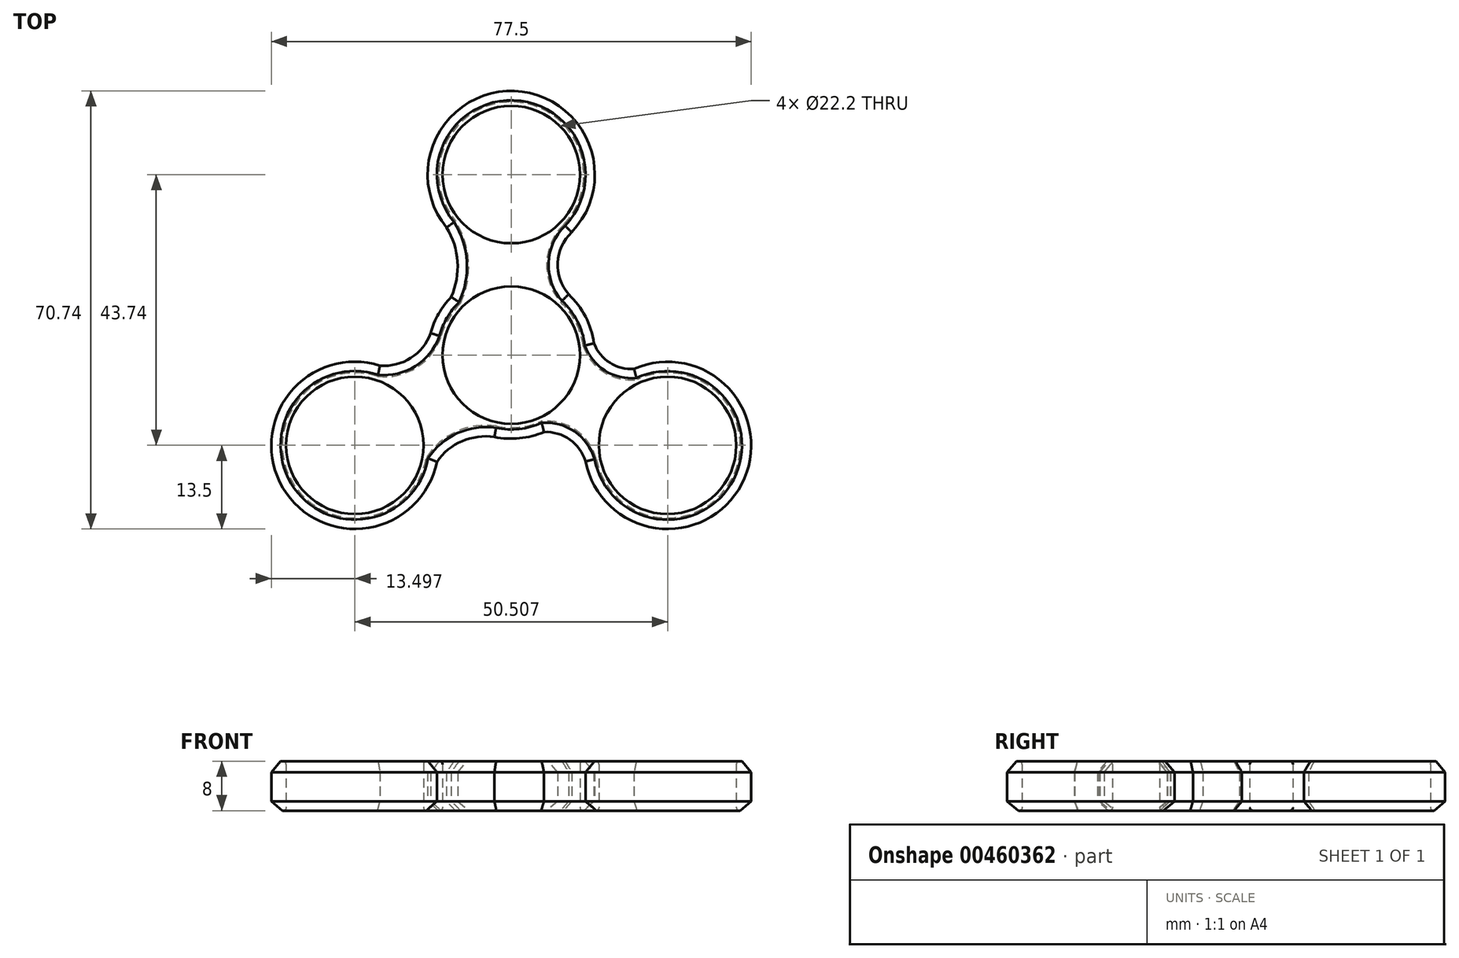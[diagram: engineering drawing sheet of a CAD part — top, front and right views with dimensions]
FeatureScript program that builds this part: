
annotation { "Feature Type Name" : "Feature", "Feature Type Description" : "" }
export const myFeature = defineFeature(function(context is Context, id is Id, definition is map)
    precondition{}
    {
        {
            var Q0;
            Q0=qCreatedBy(makeId("Top.planeOp"),FACE);
            var sketch = newSketch(context, id + "F0", { "sketchPlane" : qUnion([Q0])});
            skCircle(sketch, "E0", {"center": v(0, 0) * mm, "radius": 11.1 * mm});
            skCircle(sketch, "E1", {"center": v(0, 0) * mm, "radius": 13.5 * mm});
            skCircle(sketch, "E2", {"center": v(0, 29.16) * mm, "radius": 11.1 * mm});
            skCircle(sketch, "E3", {"center": v(0, 29.16) * mm, "radius": 13.5 * mm});
            skCircle(sketch, "E4.1.0", {"center": v(-25.25, -14.58) * mm, "radius": 11.1 * mm});
            skCircle(sketch, "E4.2.0", {"center": v(25.25, -14.58) * mm, "radius": 11.1 * mm});
            skCircle(sketch, "E5.1.0", {"center": v(-25.25, -14.58) * mm, "radius": 13.5 * mm});
            skCircle(sketch, "E5.2.0", {"center": v(25.25, -14.58) * mm, "radius": 13.5 * mm});
            skArc(sketch, "E6", {"start": v(-9.69, 9.4) * mm, "mid": v(-8.68, 15.1) * mm, "end": v(-10.44, 20.6) * mm});
            skArc(sketch, "E7", {"start": v(9.76, 19.84) * mm, "mid": v(7.53, 14.92) * mm, "end": v(9.27, 9.81) * mm});
            skArc(sketch, "E8", {"start": v(-21.2, -1.7) * mm, "mid": v(-16.22, -0.47) * mm, "end": v(-13.03, 3.55) * mm});
            skArc(sketch, "E9", {"start": v(-2.71, -13.22) * mm, "mid": v(-7.94, -13.91) * mm, "end": v(-12.02, -17.25) * mm});
            skArc(sketch, "E10", {"start": v(12, -17.17) * mm, "mid": v(9.46, -13.64) * mm, "end": v(5.28, -12.43) * mm});
            skArc(sketch, "E11", {"start": v(13.36, 1.91) * mm, "mid": v(15.92, -1.22) * mm, "end": v(19.84, -2.21) * mm});
            skSolve(sketch);
        }
        {
            var Q0;
            Q0=makeQuery(id+"F0.imprint","IMPRINT",FACE,{"disambiguationData":[TD([[makeQuery(id+"F0.imprint","IMPRINT",EDGE,{"derivedFrom":sQuery(id+"F0.wireOp",EDGE,"E2")}),-1.0]])]});
            var Q1;
            Q1=makeQuery(id+"F0.imprint","IMPRINT",FACE,{"disambiguationData":[TD([[makeQuery(id+"F0.imprint","IMPRINT",EDGE,{"derivedFrom":sQuery(id+"F0.wireOp",EDGE,"E0")}),-1.0]])]});
            var Q2;
            Q2=makeQuery(id+"F0.imprint","IMPRINT",FACE,{"disambiguationData":[TD([[makeQuery(id+"F0.imprint","IMPRINT",EDGE,{"derivedFrom":sQuery(id+"F0.wireOp",EDGE,"E4.1.0")}),-1.0]])]});
            var Q3;
            Q3=makeQuery(id+"F0.imprint","IMPRINT",FACE,{"disambiguationData":[TD([[makeQuery(id+"F0.imprint","IMPRINT",EDGE,{"derivedFrom":sQuery(id+"F0.wireOp",EDGE,"E4.2.0")}),-1.0]])]});
            var Q4;
            {var subQ0=sQuery(id+"F0.wireOp",EDGE,"E10");Q4=makeQuery(id+"F0.imprint","IMPRINT",FACE,{"disambiguationData":[TD([[makeQuery(id+"F0.imprint","IMPRINT",EDGE,{"derivedFrom":subQ0}),-1.0]])]});}
            var Q5;
            {var subQ0=sQuery(id+"F0.wireOp",EDGE,"E8");Q5=makeQuery(id+"F0.imprint","IMPRINT",FACE,{"disambiguationData":[TD([[makeQuery(id+"F0.imprint","IMPRINT",EDGE,{"derivedFrom":subQ0}),-1.0]])]});}
            var Q6;
            {var subQ0=sQuery(id+"F0.wireOp",EDGE,"E6");Q6=makeQuery(id+"F0.imprint","IMPRINT",FACE,{"disambiguationData":[TD([[makeQuery(id+"F0.imprint","IMPRINT",EDGE,{"derivedFrom":subQ0}),-1.0]])]});}
            extrude(context, id + "F1", {"entities" : qUnion([Q0, Q1, Q2, Q3, Q4, Q5, Q6]), "depth" : 8 * mm});
        }
        {
            var Q0;
            Q0=makeQuery(id+"F1.opExtrude","CAP_EDGE",EDGE,{"disambiguationData":[OSD([sQuery(id+"F0.wireOp",EDGE,"E5.1.0")])],"isStart":false});
            var Q1;
            Q1=makeQuery(id+"F1.opExtrude","CAP_EDGE",EDGE,{"disambiguationData":[OSD([sQuery(id+"F0.wireOp",EDGE,"E9")])],"isStart":false});
            var Q2;
            Q2=makeQuery(id+"F1.opExtrude","CAP_EDGE",EDGE,{"disambiguationData":[OSD([sQuery(id+"F0.wireOp",EDGE,"E8")])],"isStart":false});
            var Q3;
            {var subQ0=sQuery(id+"F0.wireOp",EDGE,"E1");Q3=makeQuery(id+"F1.opExtrude","CAP_EDGE",EDGE,{"disambiguationData":[OSD([subQ0]),TDD([makeQuery(id+"F0.imprint","IMPRINT",EDGE,{"disambiguationData":[TD([[makeQuery(id+"F0.imprint","INTERSECT",VERTEX,{"derivedFrom":[subQ0,sQuery(id+"F0.wireOp",EDGE,"E6")]}),-1.0]])],"derivedFrom":subQ0})])],"isStart":false});}
            var Q4;
            Q4=makeQuery(id+"F1.opExtrude","CAP_EDGE",EDGE,{"disambiguationData":[OSD([sQuery(id+"F0.wireOp",EDGE,"E6")])],"isStart":false});
            var Q5;
            Q5=makeQuery(id+"F1.opExtrude","CAP_EDGE",EDGE,{"disambiguationData":[OSD([sQuery(id+"F0.wireOp",EDGE,"E3")])],"isStart":false});
            var Q6;
            Q6=makeQuery(id+"F1.opExtrude","CAP_EDGE",EDGE,{"disambiguationData":[OSD([sQuery(id+"F0.wireOp",EDGE,"E7")])],"isStart":false});
            var Q7;
            {var subQ0=sQuery(id+"F0.wireOp",EDGE,"E1");Q7=makeQuery(id+"F1.opExtrude","CAP_EDGE",EDGE,{"disambiguationData":[OSD([subQ0]),TDD([makeQuery(id+"F0.imprint","IMPRINT",EDGE,{"disambiguationData":[TD([[makeQuery(id+"F0.imprint","INTERSECT",VERTEX,{"derivedFrom":[subQ0,sQuery(id+"F0.wireOp",EDGE,"E7")]}),1.0]])],"derivedFrom":subQ0})])],"isStart":false});}
            var Q8;
            Q8=makeQuery(id+"F1.opExtrude","CAP_EDGE",EDGE,{"disambiguationData":[OSD([sQuery(id+"F0.wireOp",EDGE,"E11")])],"isStart":false});
            var Q9;
            Q9=makeQuery(id+"F1.opExtrude","CAP_EDGE",EDGE,{"disambiguationData":[OSD([sQuery(id+"F0.wireOp",EDGE,"E5.2.0")])],"isStart":false});
            var Q10;
            Q10=makeQuery(id+"F1.opExtrude","CAP_EDGE",EDGE,{"disambiguationData":[OSD([sQuery(id+"F0.wireOp",EDGE,"E10")])],"isStart":false});
            var Q11;
            {var subQ0=sQuery(id+"F0.wireOp",EDGE,"E1");Q11=makeQuery(id+"F1.opExtrude","CAP_EDGE",EDGE,{"disambiguationData":[OSD([subQ0]),TDD([makeQuery(id+"F0.imprint","IMPRINT",EDGE,{"disambiguationData":[TD([[makeQuery(id+"F0.imprint","INTERSECT",VERTEX,{"derivedFrom":[subQ0,sQuery(id+"F0.wireOp",EDGE,"E9")]}),-1.0]])],"derivedFrom":subQ0})])],"isStart":false});}
            chamfer(context, id + "F2", {"entities" : qUnion([Q0, Q1, Q2, Q3, Q4, Q5, Q6, Q7, Q8, Q9, Q10, Q11]), "chamferType" : ChamferType.OFFSET_ANGLE, "width" : 1.5 * mm, "oppositeDirection" : false, "angle" : 50 * degree, "tangentPropagation" : true});
        }
        {
            var Q0;
            Q0=makeQuery(id+"F1.opExtrude","CAP_EDGE",EDGE,{"disambiguationData":[OSD([sQuery(id+"F0.wireOp",EDGE,"E3")])],"isStart":true});
            var Q1;
            Q1=makeQuery(id+"F1.opExtrude","CAP_EDGE",EDGE,{"disambiguationData":[OSD([sQuery(id+"F0.wireOp",EDGE,"E6")])],"isStart":true});
            var Q2;
            Q2=makeQuery(id+"F1.opExtrude","CAP_EDGE",EDGE,{"disambiguationData":[OSD([sQuery(id+"F0.wireOp",EDGE,"E7")])],"isStart":true});
            var Q3;
            {var subQ0=sQuery(id+"F0.wireOp",EDGE,"E1");Q3=makeQuery(id+"F1.opExtrude","CAP_EDGE",EDGE,{"disambiguationData":[OSD([subQ0]),TDD([makeQuery(id+"F0.imprint","IMPRINT",EDGE,{"disambiguationData":[TD([[makeQuery(id+"F0.imprint","INTERSECT",VERTEX,{"derivedFrom":[subQ0,sQuery(id+"F0.wireOp",EDGE,"E7")]}),1.0]])],"derivedFrom":subQ0})])],"isStart":true});}
            var Q4;
            Q4=makeQuery(id+"F1.opExtrude","CAP_EDGE",EDGE,{"disambiguationData":[OSD([sQuery(id+"F0.wireOp",EDGE,"E11")])],"isStart":true});
            var Q5;
            Q5=makeQuery(id+"F1.opExtrude","CAP_EDGE",EDGE,{"disambiguationData":[OSD([sQuery(id+"F0.wireOp",EDGE,"E5.2.0")])],"isStart":true});
            var Q6;
            Q6=makeQuery(id+"F1.opExtrude","CAP_EDGE",EDGE,{"disambiguationData":[OSD([sQuery(id+"F0.wireOp",EDGE,"E10")])],"isStart":true});
            var Q7;
            {var subQ0=sQuery(id+"F0.wireOp",EDGE,"E1");Q7=makeQuery(id+"F1.opExtrude","CAP_EDGE",EDGE,{"disambiguationData":[OSD([subQ0]),TDD([makeQuery(id+"F0.imprint","IMPRINT",EDGE,{"disambiguationData":[TD([[makeQuery(id+"F0.imprint","INTERSECT",VERTEX,{"derivedFrom":[subQ0,sQuery(id+"F0.wireOp",EDGE,"E9")]}),-1.0]])],"derivedFrom":subQ0})])],"isStart":true});}
            var Q8;
            {var subQ0=sQuery(id+"F0.wireOp",EDGE,"E1");Q8=makeQuery(id+"F1.opExtrude","CAP_EDGE",EDGE,{"disambiguationData":[OSD([subQ0]),TDD([makeQuery(id+"F0.imprint","IMPRINT",EDGE,{"disambiguationData":[TD([[makeQuery(id+"F0.imprint","INTERSECT",VERTEX,{"derivedFrom":[subQ0,sQuery(id+"F0.wireOp",EDGE,"E6")]}),-1.0]])],"derivedFrom":subQ0})])],"isStart":true});}
            var Q9;
            Q9=makeQuery(id+"F1.opExtrude","CAP_EDGE",EDGE,{"disambiguationData":[OSD([sQuery(id+"F0.wireOp",EDGE,"E8")])],"isStart":true});
            var Q10;
            Q10=makeQuery(id+"F1.opExtrude","CAP_EDGE",EDGE,{"disambiguationData":[OSD([sQuery(id+"F0.wireOp",EDGE,"E5.1.0")])],"isStart":true});
            var Q11;
            Q11=makeQuery(id+"F1.opExtrude","CAP_EDGE",EDGE,{"disambiguationData":[OSD([sQuery(id+"F0.wireOp",EDGE,"E9")])],"isStart":true});
            chamfer(context, id + "F3", {"entities" : qUnion([Q0, Q1, Q2, Q3, Q4, Q5, Q6, Q7, Q8, Q9, Q10, Q11]), "chamferType" : ChamferType.OFFSET_ANGLE, "width" : 1.5 * mm, "oppositeDirection" : false, "angle" : 50 * degree, "tangentPropagation" : true});
        }
        {
            var Q0;
            Q0=makeQuery(id+"F1.opExtrude","CAP_EDGE",EDGE,{"disambiguationData":[OSD([sQuery(id+"F0.wireOp",EDGE,"E4.2.0")])],"isStart":false});
            var Q1;
            Q1=makeQuery(id+"F1.opExtrude","CAP_EDGE",EDGE,{"disambiguationData":[OSD([sQuery(id+"F0.wireOp",EDGE,"E0")])],"isStart":false});
            var Q2;
            Q2=makeQuery(id+"F1.opExtrude","CAP_EDGE",EDGE,{"disambiguationData":[OSD([sQuery(id+"F0.wireOp",EDGE,"E4.1.0")])],"isStart":false});
            var Q3;
            Q3=makeQuery(id+"F1.opExtrude","CAP_EDGE",EDGE,{"disambiguationData":[OSD([sQuery(id+"F0.wireOp",EDGE,"E2")])],"isStart":false});
            fillet(context, id + "F4", {"entities" : qUnion([Q0, Q1, Q2, Q3]), "radius" : 0.5 * mm, "tangentPropagation" : true, "allowEdgeOverflow" : false});
        }
        {
            var Q0;
            Q0=makeQuery(id+"F1.opExtrude","CAP_EDGE",EDGE,{"disambiguationData":[OSD([sQuery(id+"F0.wireOp",EDGE,"E2")])],"isStart":true});
            var Q1;
            Q1=makeQuery(id+"F1.opExtrude","CAP_EDGE",EDGE,{"disambiguationData":[OSD([sQuery(id+"F0.wireOp",EDGE,"E4.1.0")])],"isStart":true});
            var Q2;
            Q2=makeQuery(id+"F1.opExtrude","CAP_EDGE",EDGE,{"disambiguationData":[OSD([sQuery(id+"F0.wireOp",EDGE,"E0")])],"isStart":true});
            var Q3;
            Q3=makeQuery(id+"F1.opExtrude","CAP_EDGE",EDGE,{"disambiguationData":[OSD([sQuery(id+"F0.wireOp",EDGE,"E4.2.0")])],"isStart":true});
            fillet(context, id + "F5", {"entities" : qUnion([Q0, Q1, Q2, Q3]), "radius" : 0.5 * mm, "tangentPropagation" : true, "allowEdgeOverflow" : false});
        }
    });
